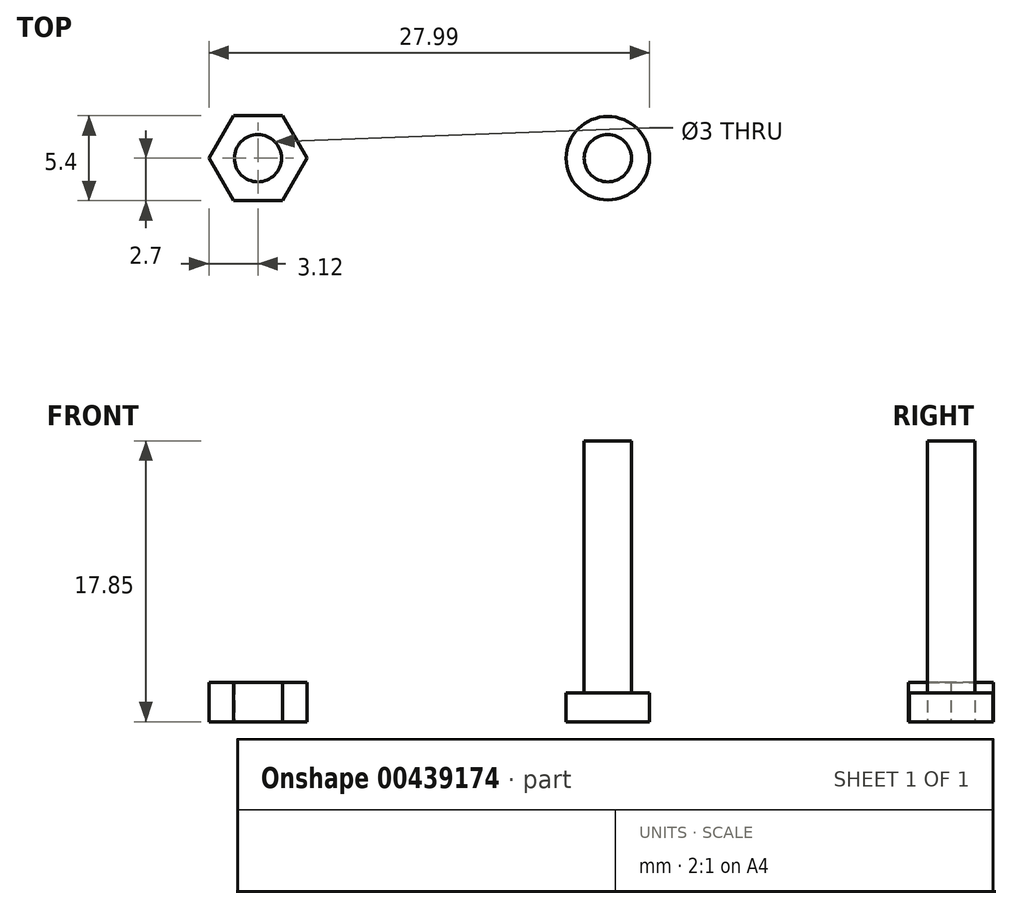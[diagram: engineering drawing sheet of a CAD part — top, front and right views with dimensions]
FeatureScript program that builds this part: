
annotation { "Feature Type Name" : "Feature", "Feature Type Description" : "" }
export const myFeature = defineFeature(function(context is Context, id is Id, definition is map)
    precondition{}
    {
        {
            var Q0;
            Q0=qCreatedBy(makeId("Top.planeOp"),FACE);
            var sketch = newSketch(context, id + "F0", { "sketchPlane" : qUnion([Q0])});
            skCircle(sketch, "E0", {"center": v(-5.47, 0) * mm, "radius": 1.5 * mm});
            skCircle(sketch, "E1.cCircle", {"center": v(-5.47, 0) * mm, "radius": 2.7 * mm, "construction": true});
            skLineSegment(sketch, "E1.0", {"start": v(-7.03, 2.7) * mm, "end": v(-3.91, 2.7) * mm});
            skLineSegment(sketch, "E1.1", {"start": v(-3.91, 2.7) * mm, "end": v(-2.35, 0) * mm});
            skLineSegment(sketch, "E1.2", {"start": v(-2.35, 0) * mm, "end": v(-3.91, -2.7) * mm});
            skLineSegment(sketch, "E1.3", {"start": v(-3.91, -2.7) * mm, "end": v(-7.03, -2.7) * mm});
            skLineSegment(sketch, "E1.4", {"start": v(-7.03, -2.7) * mm, "end": v(-8.59, 0) * mm});
            skLineSegment(sketch, "E1.5", {"start": v(-8.59, 0) * mm, "end": v(-7.03, 2.7) * mm});
            skPoint(sketch, "E1.0.midPoint", {"position": v(-5.47, 2.7) * mm});
            skSolve(sketch);
        }
        {
            var Q0;
            Q0 = qSketchRegion(id + "F0", true);
            extrude(context, id + "F1", {"entities" : qUnion([Q0]), "depth" : 2.5 * mm});
        }
        {
            var Q0;
            Q0=qCreatedBy(makeId("Top.planeOp"),FACE);
            var sketch = newSketch(context, id + "F2", { "sketchPlane" : qUnion([Q0])});
            skCircle(sketch, "E2", {"center": v(16.75, 0) * mm, "radius": 2.65 * mm});
            skSolve(sketch);
        }
        {
            var Q0;
            Q0 = qSketchRegion(id + "F2", true);
            extrude(context, id + "F3", {"entities" : qUnion([Q0]), "depth" : 1.85 * mm});
        }
        {
            var Q0;
            Q0=makeQuery(id+"F3.opExtrude","CAP_FACE",FACE,{"disambiguationData":[OSD([sQuery(id+"F2.wireOp",EDGE,"E2")])],"isStart":false});
            var sketch = newSketch(context, id + "F4", { "sketchPlane" : qUnion([Q0])});
            skCircle(sketch, "E3.0", {"center": v(16.75, 0) * mm, "radius": 2.65 * mm, "construction": true});
            skCircle(sketch, "E4", {"center": v(16.75, 0) * mm, "radius": 1.5 * mm});
            skSolve(sketch);
        }
        {
            var Q0;
            Q0 = qSketchRegion(id + "F4", true);
            extrude(context, id + "F5", {"entities" : qUnion([Q0]), "operationType" : NewBodyOperationType.ADD, "depth" : 16 * mm});
        }
    });
